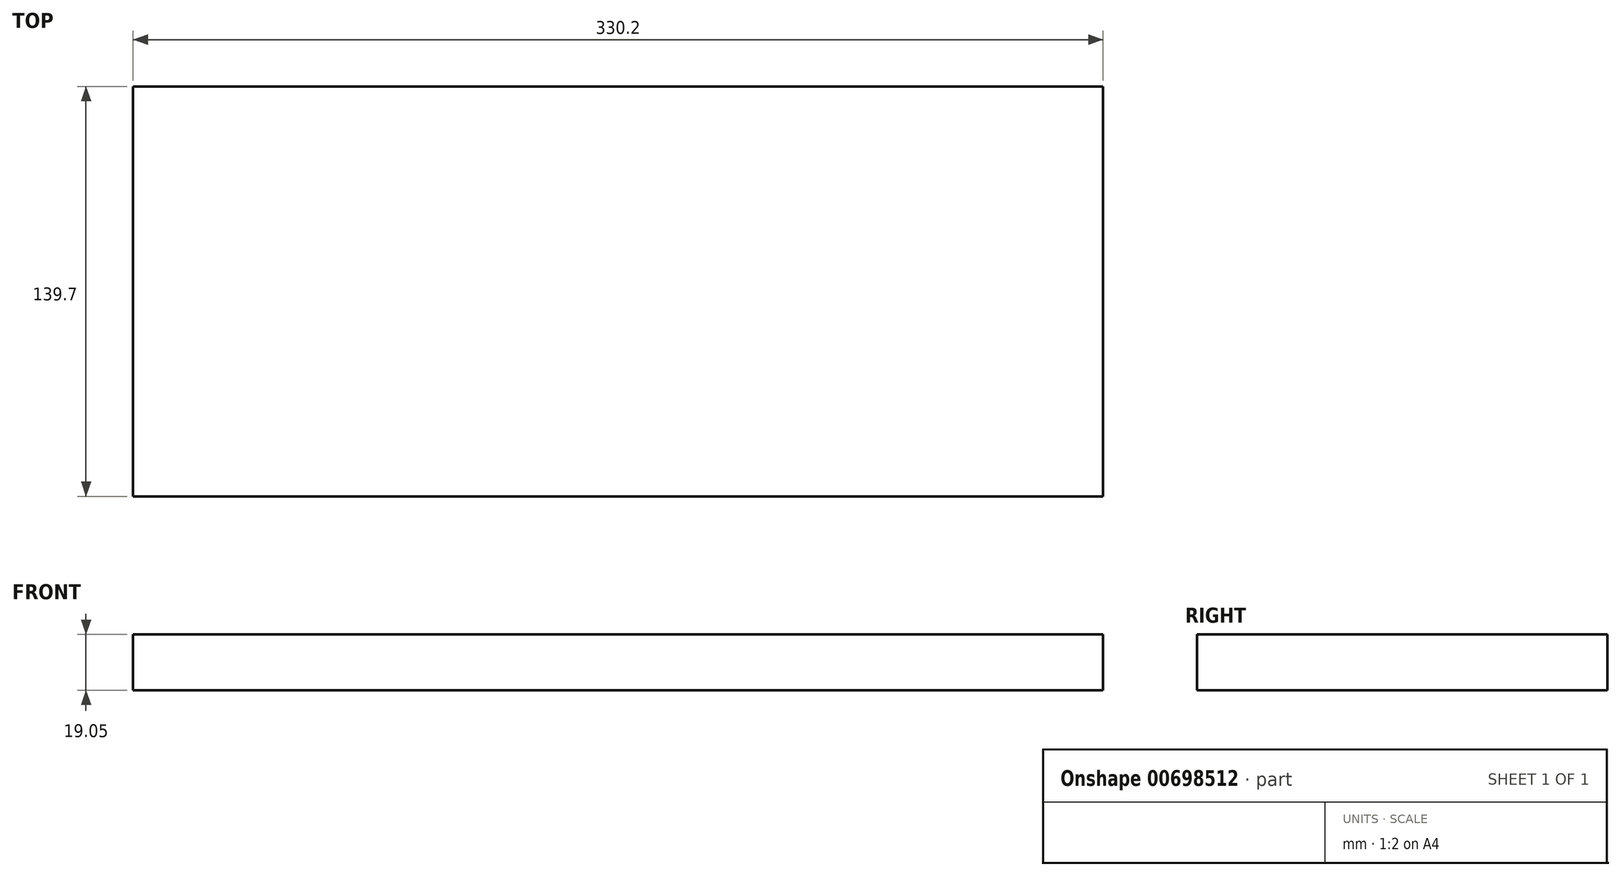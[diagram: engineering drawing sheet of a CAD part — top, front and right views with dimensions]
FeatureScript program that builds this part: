
annotation { "Feature Type Name" : "Feature", "Feature Type Description" : "" }
export const myFeature = defineFeature(function(context is Context, id is Id, definition is map)
    precondition{}
    {
        {
            var Q0;
            Q0=qCreatedBy(makeId("Top.planeOp"),FACE);
            var sketch = newSketch(context, id + "F0", { "sketchPlane" : qUnion([Q0])});
            skLineSegment(sketch, "E0.bottom", {"start": v(-142.15, -69.28) * mm, "end": v(188.05, -69.28) * mm});
            skLineSegment(sketch, "E0.top", {"start": v(-142.15, 70.42) * mm, "end": v(188.05, 70.42) * mm});
            skLineSegment(sketch, "E0.left", {"start": v(-142.15, -69.28) * mm, "end": v(-142.15, 70.42) * mm});
            skLineSegment(sketch, "E0.right", {"start": v(188.05, -69.28) * mm, "end": v(188.05, 70.42) * mm});
            skSolve(sketch);
        }
        {
            var Q0;
            Q0 = qSketchRegion(id + "F0", true);
            extrude(context, id + "F1", {"entities" : qUnion([Q0]), "depth" : 19.05 * mm, "offsetDistance" : 25.4 * mm});
        }
    });
